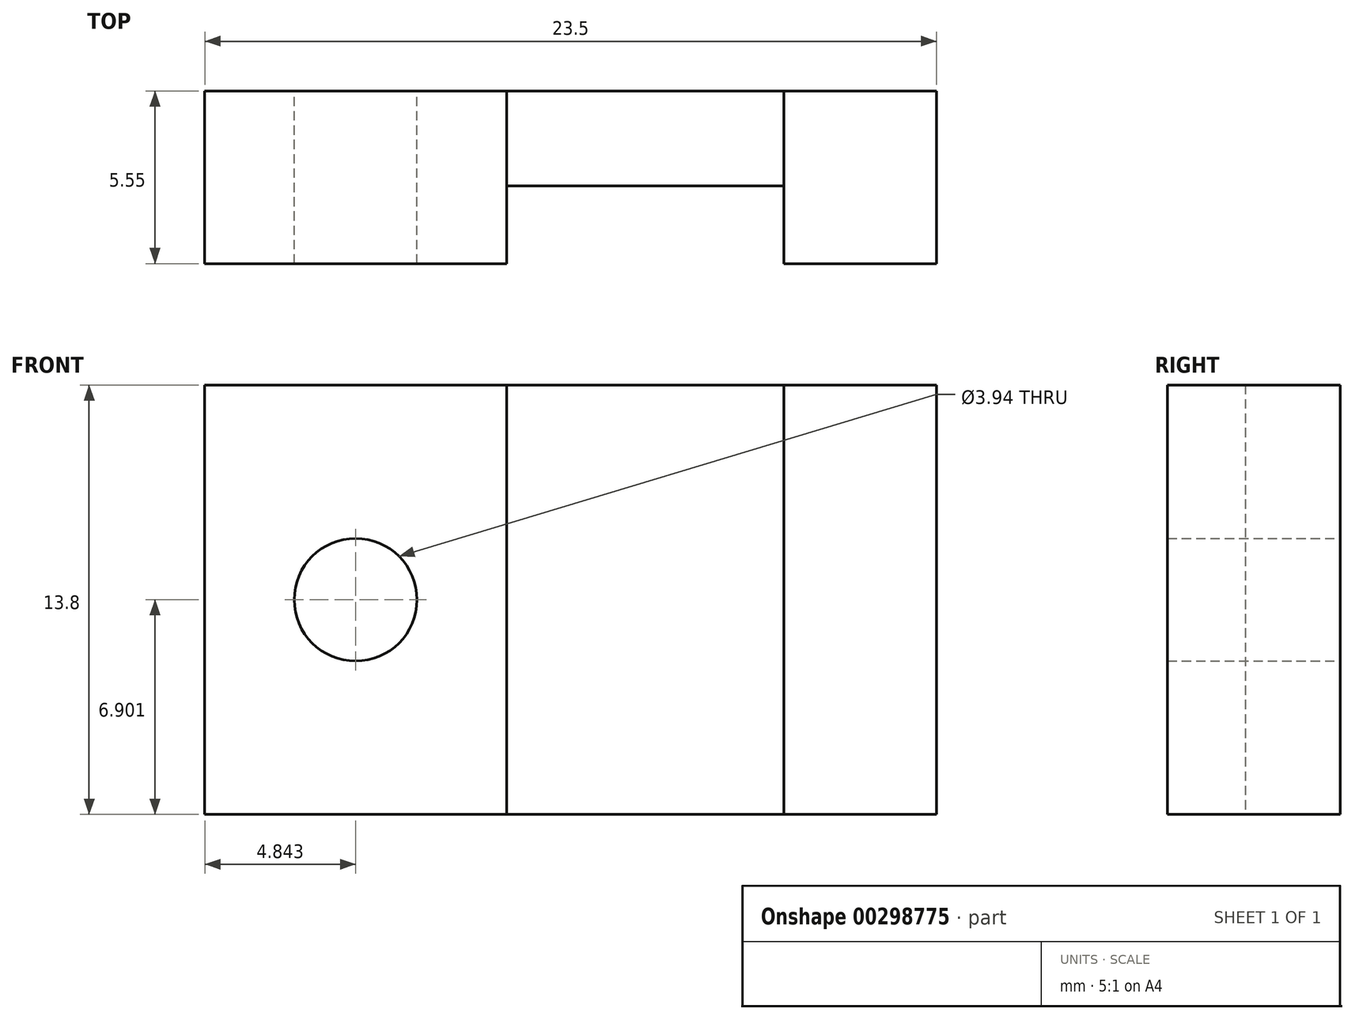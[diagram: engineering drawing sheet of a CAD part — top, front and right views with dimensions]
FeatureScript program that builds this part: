
annotation { "Feature Type Name" : "Feature", "Feature Type Description" : "" }
export const myFeature = defineFeature(function(context is Context, id is Id, definition is map)
    precondition{}
    {
        {
            var Q0;
            Q0=qCreatedBy(makeId("Front.planeOp"),FACE);
            var sketch = newSketch(context, id + "F0", { "sketchPlane" : qUnion([Q0])});
            skLineSegment(sketch, "E0", {"start": v(-57.2, 41.83) * mm, "end": v(-33.7, 41.83) * mm});
            skLineSegment(sketch, "E1", {"start": v(-57.2, 41.83) * mm, "end": v(-57.2, 28.03) * mm});
            skLineSegment(sketch, "E2", {"start": v(-57.2, 28.03) * mm, "end": v(-33.7, 28.03) * mm});
            skLineSegment(sketch, "E3", {"start": v(-33.7, 28.03) * mm, "end": v(-33.7, 41.83) * mm});
            skPoint(sketch, "E4", {"position": v(-47.5, 41.83) * mm});
            skLineSegment(sketch, "E5", {"start": v(-47.5, 41.83) * mm, "end": v(-47.5, 28.03) * mm});
            skPoint(sketch, "E6", {"position": v(-38.6, 41.83) * mm});
            skLineSegment(sketch, "E7", {"start": v(-38.6, 41.83) * mm, "end": v(-38.6, 28.03) * mm});
            skLineSegment(sketch, "E8", {"start": v(-57.2, 41.83) * mm, "end": v(-47.5, 41.83) * mm});
            skPoint(sketch, "E9", {"position": v(-57.2, 36.94) * mm});
            skCircle(sketch, "E10", {"center": v(-52.35, 34.93) * mm, "radius": 1.97 * mm});
            skSolve(sketch);
        }
        {
            var Q0;
            {var subQ1=sQuery(id+"F0.wireOp",EDGE,"E1");Q0=makeQuery(id+"F0.imprint","IMPRINT",FACE,{"disambiguationData":[TD([[makeQuery(id+"F0.imprint","IMPRINT",EDGE,{"derivedFrom":subQ1}),1.0]])]});}
            var Q1;
            {var subQ0=sQuery(id+"F0.wireOp",EDGE,"E3");Q1=makeQuery(id+"F0.imprint","IMPRINT",FACE,{"disambiguationData":[TD([[makeQuery(id+"F0.imprint","IMPRINT",EDGE,{"derivedFrom":subQ0}),1.0]])]});}
            extrude(context, id + "F1", {"entities" : qUnion([Q0, Q1]), "depth" : 5.55 * mm});
        }
        {
            var Q0;
            {var subQ0=sQuery(id+"F0.wireOp",EDGE,"E5");Q0=makeQuery(id+"F0.imprint","IMPRINT",FACE,{"disambiguationData":[TD([[makeQuery(id+"F0.imprint","IMPRINT",EDGE,{"derivedFrom":subQ0}),1.0]])]});}
            extrude(context, id + "F2", {"entities" : qUnion([Q0]), "depth" : 3.05 * mm});
        }
    });
